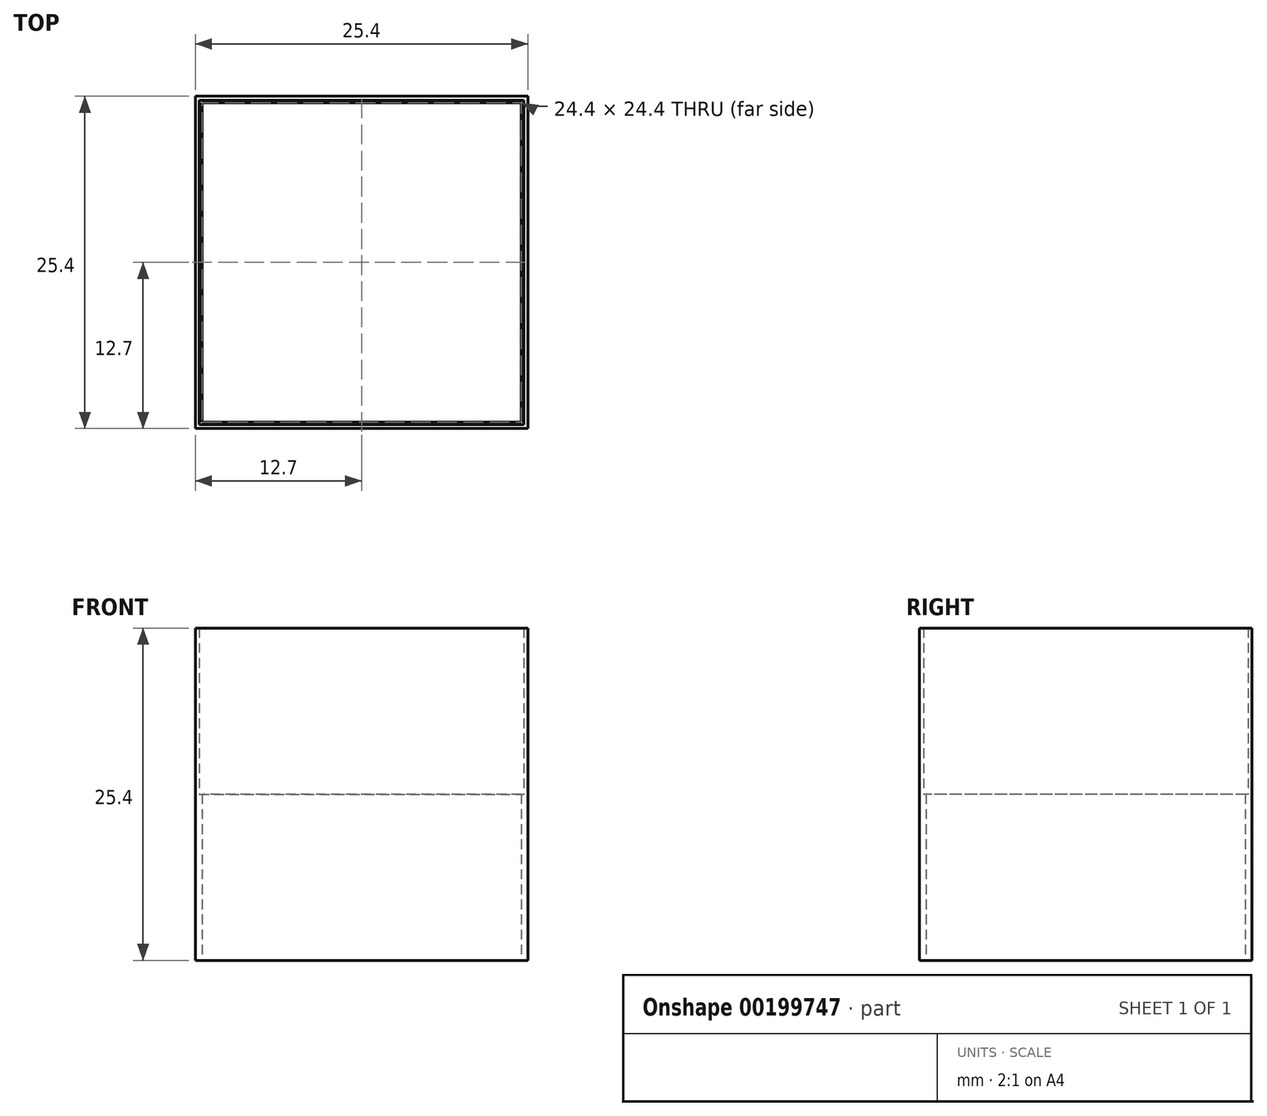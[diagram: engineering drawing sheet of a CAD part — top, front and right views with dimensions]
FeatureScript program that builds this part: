
annotation { "Feature Type Name" : "Feature", "Feature Type Description" : "" }
export const myFeature = defineFeature(function(context is Context, id is Id, definition is map)
    precondition{}
    {
        {
            var Q0;
            Q0=qCreatedBy(makeId("Top.planeOp"),FACE);
            var sketch = newSketch(context, id + "F0", { "sketchPlane" : qUnion([Q0])});
            skLineSegment(sketch, "E0.bottom", {"start": v(12.7, 12.7) * mm, "end": v(-12.7, 12.7) * mm});
            skLineSegment(sketch, "E0.top", {"start": v(12.7, -12.7) * mm, "end": v(-12.7, -12.7) * mm});
            skLineSegment(sketch, "E0.left", {"start": v(12.7, 12.7) * mm, "end": v(12.7, -12.7) * mm});
            skLineSegment(sketch, "E0.right", {"start": v(-12.7, 12.7) * mm, "end": v(-12.7, -12.7) * mm});
            skPoint(sketch, "E0.middle", {"position": v(0, 0) * mm});
            skLineSegment(sketch, "E1.bottom", {"start": v(12.2, 12.2) * mm, "end": v(-12.2, 12.2) * mm});
            skLineSegment(sketch, "E1.top", {"start": v(12.2, -12.2) * mm, "end": v(-12.2, -12.2) * mm});
            skLineSegment(sketch, "E1.left", {"start": v(12.2, 12.2) * mm, "end": v(12.2, -12.2) * mm});
            skLineSegment(sketch, "E1.right", {"start": v(-12.2, 12.2) * mm, "end": v(-12.2, -12.2) * mm});
            skSolve(sketch);
        }
        {
            var Q0;
            Q0 = qSketchRegion(id + "F0", true);
            extrude(context, id + "F1", {"entities" : qUnion([Q0]), "depth" : 12.7 * mm});
        }
        {
            var Q0;
            Q0=makeQuery(id+"F1.opExtrude","CAP_FACE",FACE,{"disambiguationData":[OSD([sQuery(id+"F0.wireOp",EDGE,"E0.bottom"),sQuery(id+"F0.wireOp",EDGE,"E0.top"),sQuery(id+"F0.wireOp",EDGE,"E0.left"),sQuery(id+"F0.wireOp",EDGE,"E0.right"),sQuery(id+"F0.wireOp",EDGE,"E1.bottom"),sQuery(id+"F0.wireOp",EDGE,"E1.top"),sQuery(id+"F0.wireOp",EDGE,"E1.left"),sQuery(id+"F0.wireOp",EDGE,"E1.right")])],"isStart":false});
            var sketch = newSketch(context, id + "F2", { "sketchPlane" : qUnion([Q0])});
            skPoint(sketch, "E2.middle", {"position": v(0, 0) * mm});
            skLineSegment(sketch, "E3.bottom", {"start": v(-12.4, 12.4) * mm, "end": v(12.4, 12.4) * mm});
            skLineSegment(sketch, "E3.top", {"start": v(-12.4, -12.4) * mm, "end": v(12.4, -12.4) * mm});
            skLineSegment(sketch, "E3.left", {"start": v(-12.4, 12.4) * mm, "end": v(-12.4, -12.4) * mm});
            skLineSegment(sketch, "E3.right", {"start": v(12.4, 12.4) * mm, "end": v(12.4, -12.4) * mm});
            skLineSegment(sketch, "E4.bottom", {"start": v(12.7, 12.7) * mm, "end": v(-12.7, 12.7) * mm});
            skLineSegment(sketch, "E4.top", {"start": v(12.7, -12.7) * mm, "end": v(-12.7, -12.7) * mm});
            skLineSegment(sketch, "E4.left", {"start": v(12.7, 12.7) * mm, "end": v(12.7, -12.7) * mm});
            skLineSegment(sketch, "E4.right", {"start": v(-12.7, 12.7) * mm, "end": v(-12.7, -12.7) * mm});
            skSolve(sketch);
        }
        {
            var Q0;
            Q0=makeQuery(id+"F2.imprint","IMPRINT",FACE,{"disambiguationData":[TD([[makeQuery(id+"F2.imprint","IMPRINT",EDGE,{"derivedFrom":sQuery(id+"F2.wireOp",EDGE,"E3.bottom")}),1.0]])]});
            extrude(context, id + "F3", {"entities" : qUnion([Q0]), "operationType" : NewBodyOperationType.ADD, "depth" : 12.7 * mm});
        }
    });
